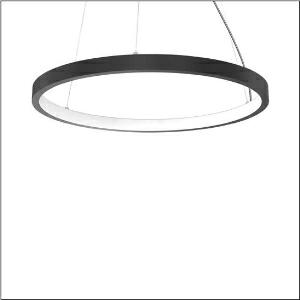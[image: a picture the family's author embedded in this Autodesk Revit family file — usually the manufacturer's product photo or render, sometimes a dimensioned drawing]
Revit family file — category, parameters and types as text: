
# Revit family: silica_21_ring-i_5pjbi4d1104a
name_source: partatom
category: Lighting Fixtures
units: mm (PartAtom-declared; Revit-internal decimal feet)

## family parameters
Cut with Voids When Loaded = No
Host = Face
Light Source = No
Part Type = Normal
Room Calculation Point = No
Round Connector Dimension = Use Diameter
Shared = No

## types (1)
- Silica 21 Ring-I (1 x LED, 8460 lm, 140 W, 3000K)
    Apparent Load = 140 VA
    CIE Flux Codes = 22 48 76 50 101
    Color Rendering = 80
    Color Temperature = 3000K
    Default Elevation = 1800 mm
    Description = Silica 21 Ring-I, suspended luminaire, of PMMA, frosted, light emission: inner ring side luminous distribution, primary light characteristic: symmetric, installation type: suspended mounting, LED, rated luminous flux: 8.460lm, luminous efficacy: 61lm/W, light colour: 830, colour temperature: 3000K, control gear: DALI 2, with terminal, 5-pole, mains connection: 230V, AC/DC, 0/50..60Hz, rated input power: 140W, housing, of extruded aluminium section, jet black (RAL 9005), diameter: 1.470mm, ceiling canopy, jet black (RAL 9005), protection rating (lamp compartment): IP40, insulation class (complete): insulation class I (protective earthing), certification: CE, impact resistance: IK02, permissible operating ambient temperature: 0..+35°C, packaging unit: 1 piece
    Height = 48 mm  [stored 0.15748 ft]
    Lamp = 1 x LED
    Lamp Light Flux = 8460 lm
    Lamp Power = 140 W
    Lamp count = 1
    Length = 1470 mm
    Luminous efficacy = 60 lm/W
    Manufacturer = Siteco
    ModVariant = No
    Model = 5PJBI4D1104A
    Mounting Place = Ceiling
    Mounting Type = Pendant
    Number of Poles = 1
    OnlyDefault = Yes
    Power Factor = 1
    Product Name = Silica 21 Ring-I
    Product group = suspended luminaire
    ProductGroupID = 904
    Protection Class = Protection class I
    Protection Degree = IP 40
    RLX_Detail_Level = 1
    RLX_Emergency_Light_Flux = 0 lm
    RLX_Emergency_Type = 0
    RLX_Emergency_Type_DB = No
    RlxData = <blob elided: 20381 chars, md5=0bf7d079>
    Socket = socket
    Standby Power = 0 W
    System Light Flux = 8460 lm
    System Power = 140 W
    Type Comments = Product without accessories
    Type Image = l_1258373.jpg
    URL = http://relux.com
    VarID = ---
    Voltage = 0 V
    Weight = 0.00 kg
    Width = 0 mm  [stored 0 ft]

note: [stored X ft] marks values corroborated as IEEE doubles in the binary element streams (Revit-internal decimal feet)

## geometry (parser evidence)
native form markers: Blend x4, Sweep x11
no freeform markers — native parametric forms only
